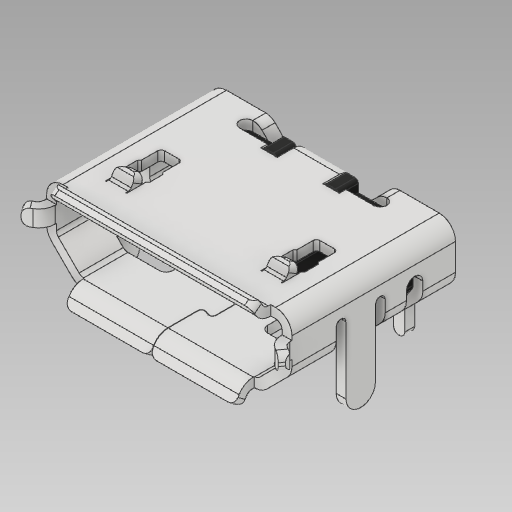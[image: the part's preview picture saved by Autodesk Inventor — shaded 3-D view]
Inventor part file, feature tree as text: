
AUTODESK INVENTOR PART (.ipt)
format: ipt  version: 2020 (Build 240168000, 168)  size: 830,464 bytes
history: native  units: in
note: dims shown in document units (in); Inventor stores cm internally (conversion verified against a paired STEP export)
features: other x5, fillet x2
ambient origin geometry x8: Origin, YZ Plane, XZ Plane, XY Plane, X Axis, Y Axis, Z Axis, Center Point
bodies: Solid1 (feature_tree), Solid2 (feature_tree), Solid3 (feature_tree), Solid4 (feature_tree), Solid5 (feature_tree), Solid6 (feature_tree), Solid7 (feature_tree)
feature tree (7):
  other  "Cut-Extrude13"
  fillet  "Fillet14"  [1 undecoded]
  other  "LPattern1[1]"
  other  "LPattern1[2]"
  other  "LPattern1[3]"
  other  "LPattern1[4]"
  fillet  "Fillet11"  [1 undecoded]
note: 2 required parameter values undecoded (feature->parameter linkage not recoverable at this tier; creation-order binding heuristic only, values carry confidence <= 0.55)
